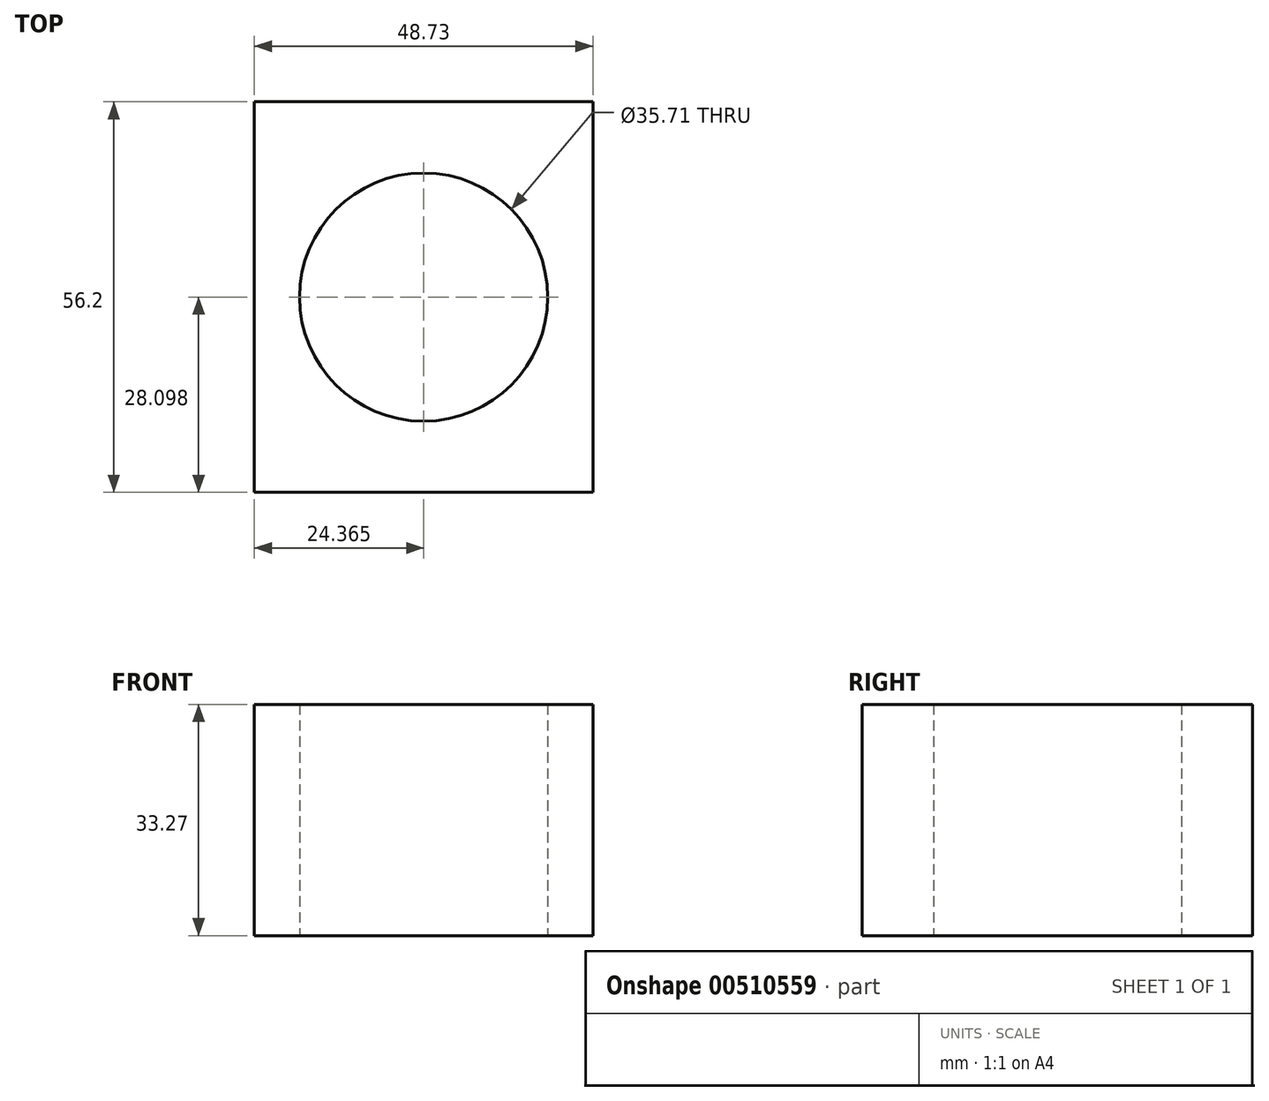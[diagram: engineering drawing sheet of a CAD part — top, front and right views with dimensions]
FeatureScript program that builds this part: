
annotation { "Feature Type Name" : "Feature", "Feature Type Description" : "" }
export const myFeature = defineFeature(function(context is Context, id is Id, definition is map)
    precondition{}
    {
        {
            var Q0;
            Q0=qCreatedBy(makeId("Top.planeOp"),FACE);
            var sketch = newSketch(context, id + "F0", { "sketchPlane" : qUnion([Q0])});
            skLineSegment(sketch, "E0.bottom", {"start": v(-15.67, -20) * mm, "end": v(33.06, -20) * mm});
            skLineSegment(sketch, "E0.top", {"start": v(-15.67, 36.2) * mm, "end": v(33.06, 36.2) * mm});
            skLineSegment(sketch, "E0.left", {"start": v(-15.67, -20) * mm, "end": v(-15.67, 36.2) * mm});
            skLineSegment(sketch, "E0.right", {"start": v(33.06, -20) * mm, "end": v(33.06, 36.2) * mm});
            skCircle(sketch, "E1", {"center": v(8.7, 8.1) * mm, "radius": 17.86 * mm});
            skPoint(sketch, "E1.centerSnap0", {"position": v(8.7, -20) * mm});
            skPoint(sketch, "E1.centerSnap1", {"position": v(-15.67, 8.1) * mm});
            skSolve(sketch);
        }
        {
            var Q0;
            Q0=makeQuery(id+"F0.imprint","IMPRINT",FACE,{"disambiguationData":[TD([[makeQuery(id+"F0.imprint","IMPRINT",EDGE,{"derivedFrom":sQuery(id+"F0.wireOp",EDGE,"E0.bottom")}),1.0]])]});
            extrude(context, id + "F1", {"entities" : qUnion([Q0]), "depth" : 33.27 * mm});
        }
    });
